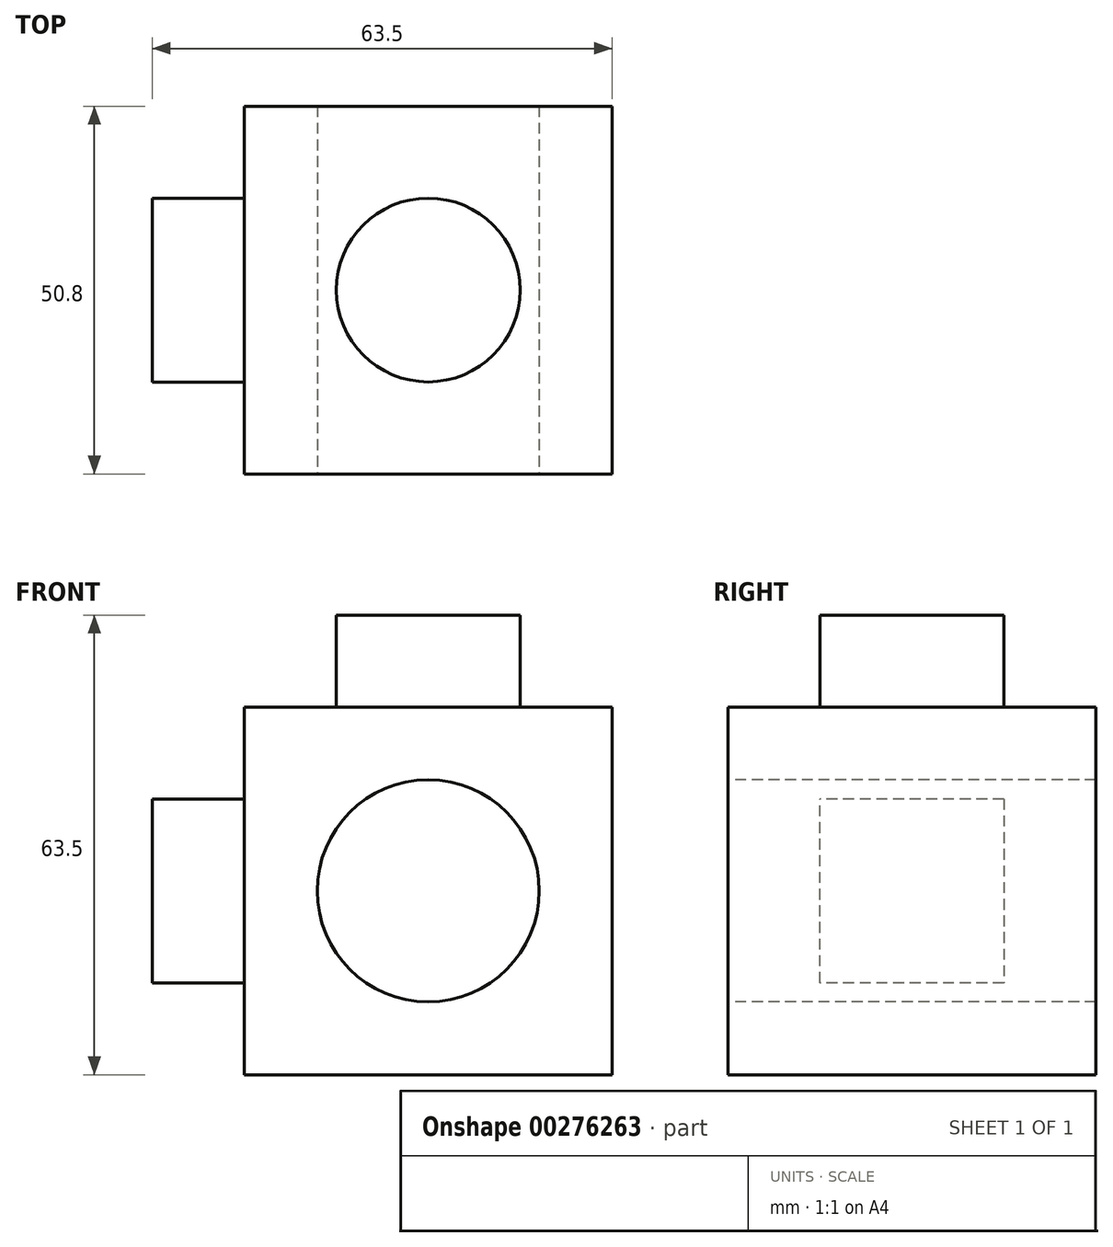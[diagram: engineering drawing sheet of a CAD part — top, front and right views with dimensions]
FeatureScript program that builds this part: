
annotation { "Feature Type Name" : "Feature", "Feature Type Description" : "" }
export const myFeature = defineFeature(function(context is Context, id is Id, definition is map)
    precondition{}
    {
        {
            var Q0;
            Q0=qCreatedBy(makeId("Front.planeOp"),FACE);
            var sketch = newSketch(context, id + "F0", { "sketchPlane" : qUnion([Q0])});
            skLineSegment(sketch, "E0", {"start": v(-63.69, 0) * mm, "end": v(-63.69, 50.8) * mm});
            skLineSegment(sketch, "E1", {"start": v(-63.69, 50.8) * mm, "end": v(-12.89, 50.8) * mm});
            skLineSegment(sketch, "E2", {"start": v(-12.89, 50.8) * mm, "end": v(-12.89, 0) * mm});
            skLineSegment(sketch, "E3", {"start": v(-12.89, 0) * mm, "end": v(-63.69, 0) * mm});
            skSolve(sketch);
        }
        {
            var Q0;
            Q0 = qSketchRegion(id + "F0", true);
            extrude(context, id + "F1", {"entities" : qUnion([Q0]), "depth" : 50.8 * mm});
        }
        {
            var Q0;
            Q0=makeQuery(id+"F1.opExtrude","CAP_FACE",FACE,{"disambiguationData":[OSD([sQuery(id+"F0.wireOp",EDGE,"E0"),sQuery(id+"F0.wireOp",EDGE,"E1"),sQuery(id+"F0.wireOp",EDGE,"E2"),sQuery(id+"F0.wireOp",EDGE,"E3")])],"isStart":false});
            var sketch = newSketch(context, id + "F2", { "sketchPlane" : qUnion([Q0])});
            skCircle(sketch, "E4", {"center": v(-38.29, 25.4) * mm, "radius": 15.33 * mm});
            skSolve(sketch);
        }
        {
            var Q0;
            Q0 = qSketchRegion(id + "F2", true);
            extrude(context, id + "F3", {"entities" : qUnion([Q0]), "operationType" : NewBodyOperationType.REMOVE, "oppositeDirection" : true, "depth" : 50.8 * mm});
        }
        {
            var Q0;
            Q0=makeQuery(id+"F1.opExtrude","SWEPT_FACE",FACE,{"disambiguationData":[OSD([sQuery(id+"F0.wireOp",EDGE,"E1")])]});
            var sketch = newSketch(context, id + "F4", { "sketchPlane" : qUnion([Q0])});
            skCircle(sketch, "E5", {"center": v(-38.29, -25.4) * mm, "radius": 12.7 * mm});
            skSolve(sketch);
        }
        {
            var Q0;
            Q0 = qSketchRegion(id + "F4", true);
            extrude(context, id + "F5", {"entities" : qUnion([Q0]), "operationType" : NewBodyOperationType.ADD, "depth" : 12.7 * mm});
        }
        {
            var Q0;
            Q0=makeQuery(id+"F1.opExtrude","SWEPT_FACE",FACE,{"disambiguationData":[OSD([sQuery(id+"F0.wireOp",EDGE,"E0")])]});
            var sketch = newSketch(context, id + "F6", { "sketchPlane" : qUnion([Q0])});
            skLineSegment(sketch, "E6", {"start": v(12.7, 38.1) * mm, "end": v(12.7, 12.7) * mm});
            skLineSegment(sketch, "E7", {"start": v(12.7, 38.1) * mm, "end": v(38.1, 38.1) * mm});
            skLineSegment(sketch, "E8", {"start": v(12.7, 12.7) * mm, "end": v(38.1, 12.7) * mm});
            skLineSegment(sketch, "E9", {"start": v(38.1, 12.7) * mm, "end": v(38.1, 38.1) * mm});
            skSolve(sketch);
        }
        {
            var Q0;
            Q0 = qSketchRegion(id + "F6", true);
            extrude(context, id + "F7", {"entities" : qUnion([Q0]), "operationType" : NewBodyOperationType.ADD, "depth" : 12.7 * mm});
        }
    });
